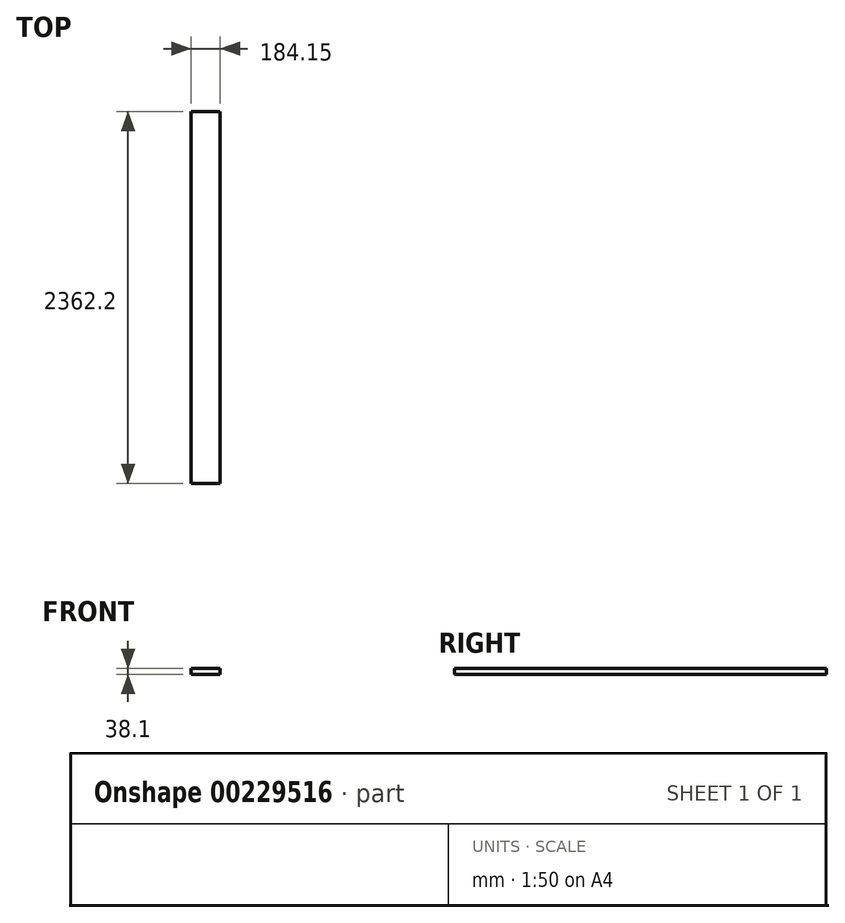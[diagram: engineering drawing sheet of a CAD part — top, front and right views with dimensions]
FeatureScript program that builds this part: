
annotation { "Feature Type Name" : "Feature", "Feature Type Description" : "" }
export const myFeature = defineFeature(function(context is Context, id is Id, definition is map)
    precondition{}
    {
        {
            var Q0;
            Q0=qCreatedBy(makeId("Front.planeOp"),FACE);
            var sketch = newSketch(context, id + "F0", { "sketchPlane" : qUnion([Q0])});
            skLineSegment(sketch, "E0.bottom", {"start": v(0, 0) * mm, "end": v(184.15, 0) * mm});
            skLineSegment(sketch, "E0.top", {"start": v(0, -38.1) * mm, "end": v(184.15, -38.1) * mm});
            skLineSegment(sketch, "E0.left", {"start": v(0, 0) * mm, "end": v(0, -38.1) * mm});
            skLineSegment(sketch, "E0.right", {"start": v(184.15, 0) * mm, "end": v(184.15, -38.1) * mm});
            skSolve(sketch);
        }
        {
            var Q0;
            Q0=qSketchRegion(id+"F0",true);
            extrude(context, id + "F1", {"entities" : qUnion([Q0]), "depth" : 2362.2 * mm});
        }
    });
